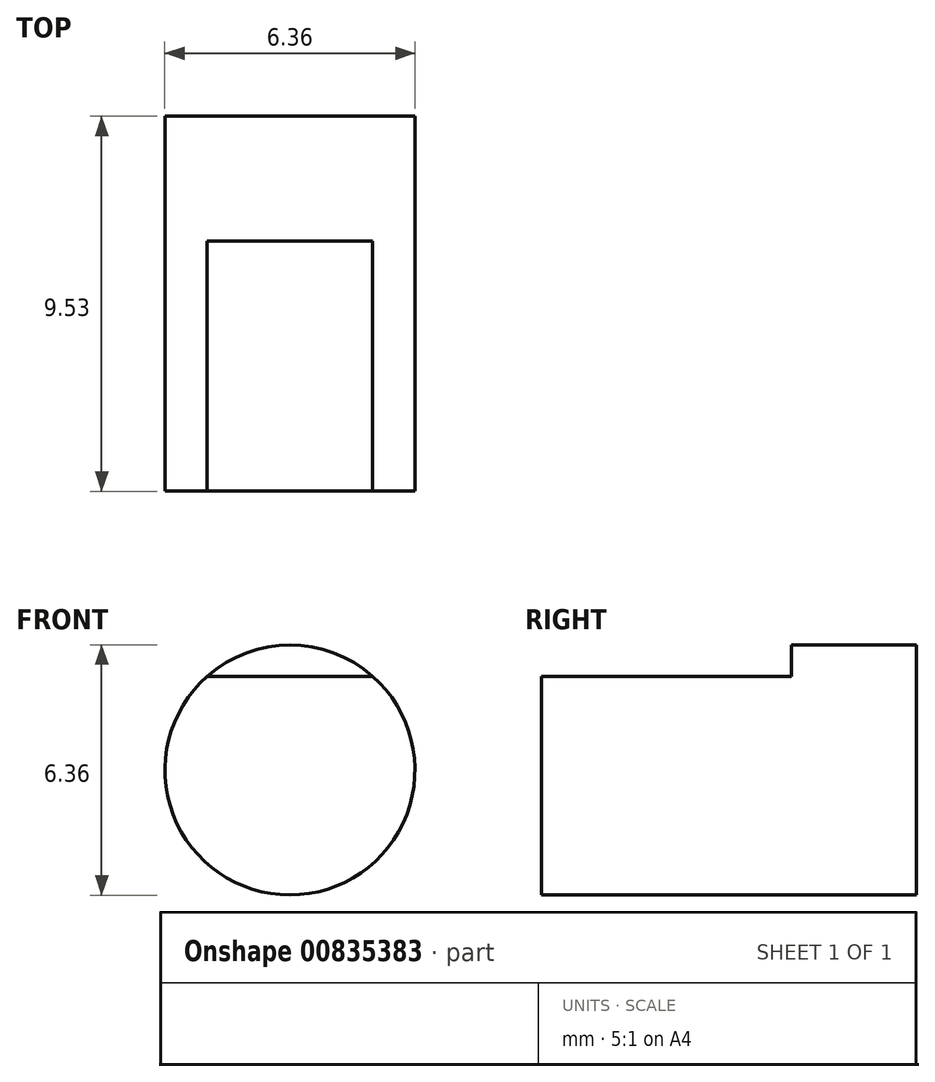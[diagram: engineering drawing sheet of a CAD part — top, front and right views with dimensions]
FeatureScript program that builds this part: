
annotation { "Feature Type Name" : "Feature", "Feature Type Description" : "" }
export const myFeature = defineFeature(function(context is Context, id is Id, definition is map)
    precondition{}
    {
        {
            var Q0;
            Q0=qCreatedBy(makeId("Front.planeOp"),FACE);
            var sketch = newSketch(context, id + "F0", { "sketchPlane" : qUnion([Q0])});
            skCircle(sketch, "E0", {"center": v(0, 0) * mm, "radius": 3.18 * mm});
            skSolve(sketch);
        }
        {
            var Q0;
            Q0=makeQuery(id+"F0.imprint","IMPRINT",FACE,{"disambiguationData":[TD([[makeQuery(id+"F0.imprint","IMPRINT",EDGE,{"derivedFrom":sQuery(id+"F0.wireOp",EDGE,"E0")}),1.0]])]});
            extrude(context, id + "F1", {"entities" : qUnion([Q0]), "depth" : 9.52 * mm, "offsetDistance" : 25.4 * mm});
        }
        {
            var Q0;
            Q0=makeQuery(id+"F1.opExtrude","CAP_FACE",FACE,{"disambiguationData":[OSD([sQuery(id+"F0.wireOp",EDGE,"E0")])],"isStart":false});
            var sketch = newSketch(context, id + "F2", { "sketchPlane" : qUnion([Q0])});
            skLineSegment(sketch, "E1", {"start": v(-2.1, 2.38) * mm, "end": v(2.1, 2.38) * mm});
            skArc(sketch, "E2", {"start": v(2.1, 2.38) * mm, "mid": v(0, 3.18) * mm, "end": v(-2.1, 2.38) * mm});
            skSolve(sketch);
        }
        {
            var Q0;
            Q0=makeQuery(id+"F2.imprint","IMPRINT",FACE,{"disambiguationData":[TD([[makeQuery(id+"F2.imprint","IMPRINT",EDGE,{"derivedFrom":sQuery(id+"F2.wireOp",EDGE,"E1")}),1.0]])]});
            extrude(context, id + "F3", {"entities" : qUnion([Q0]), "operationType" : NewBodyOperationType.REMOVE, "oppositeDirection" : true, "depth" : 6.35 * mm, "offsetDistance" : 25.4 * mm});
        }
    });
